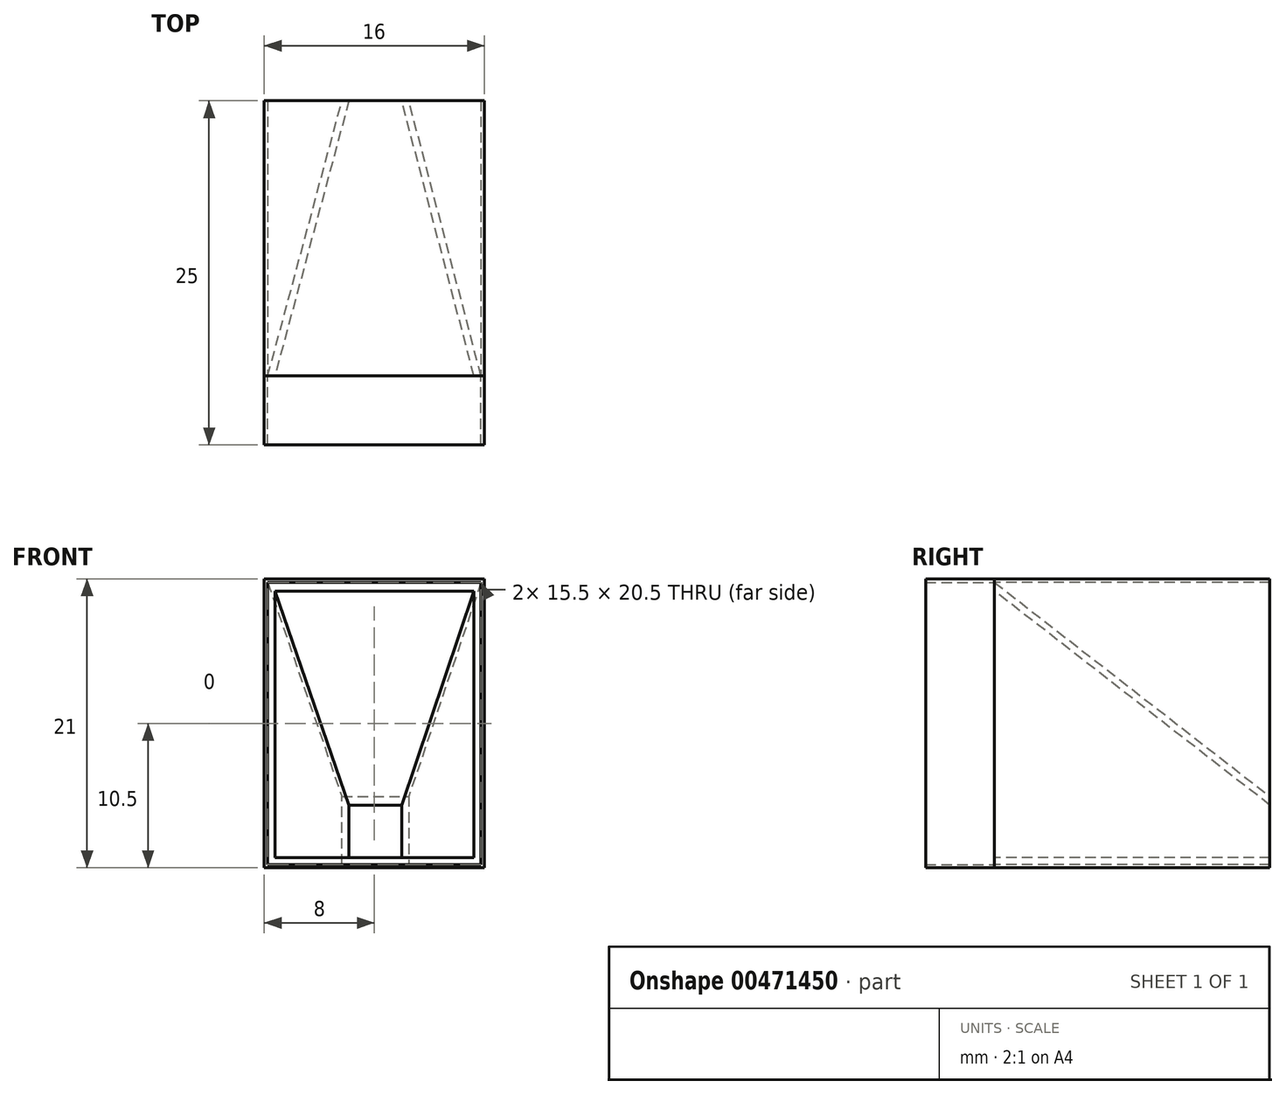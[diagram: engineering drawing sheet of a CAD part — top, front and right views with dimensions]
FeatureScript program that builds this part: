
annotation { "Feature Type Name" : "Feature", "Feature Type Description" : "" }
export const myFeature = defineFeature(function(context is Context, id is Id, definition is map)
    precondition{}
    {
        {
            var Q0;
            Q0=qCreatedBy(makeId("Front.planeOp"),FACE);
            var sketch = newSketch(context, id + "F0", { "sketchPlane" : qUnion([Q0])});
            skLineSegment(sketch, "E0.bottom", {"start": v(-8, 10.5) * mm, "end": v(8, 10.5) * mm});
            skLineSegment(sketch, "E0.top", {"start": v(-8, -10.5) * mm, "end": v(8, -10.5) * mm});
            skLineSegment(sketch, "E0.left", {"start": v(-8, 10.5) * mm, "end": v(-8, -10.5) * mm});
            skLineSegment(sketch, "E0.right", {"start": v(8, 10.5) * mm, "end": v(8, -10.5) * mm});
            skPoint(sketch, "E0.middle", {"position": v(0, 0) * mm});
            skLineSegment(sketch, "E1.bottom", {"start": v(-7.75, -10.25) * mm, "end": v(7.75, -10.25) * mm});
            skLineSegment(sketch, "E1.top", {"start": v(-7.75, 10.25) * mm, "end": v(7.75, 10.25) * mm});
            skLineSegment(sketch, "E1.left", {"start": v(-7.75, -10.25) * mm, "end": v(-7.75, 10.25) * mm});
            skLineSegment(sketch, "E1.right", {"start": v(7.75, -10.25) * mm, "end": v(7.75, 10.25) * mm});
            skSolve(sketch);
        }
        {
            var Q0;
            Q0=makeQuery(id+"F0.imprint","IMPRINT",FACE,{"disambiguationData":[TD([[makeQuery(id+"F0.imprint","IMPRINT",EDGE,{"derivedFrom":sQuery(id+"F0.wireOp",EDGE,"E0.bottom")}),-1.0]])]});
            extrude(context, id + "F1", {"entities" : qUnion([Q0]), "depth" : 5 * mm});
        }
        {
            var Q0;
            Q0=makeQuery(id+"F1.opExtrude","CAP_FACE",FACE,{"disambiguationData":[OSD([sQuery(id+"F0.wireOp",EDGE,"E0.bottom"),sQuery(id+"F0.wireOp",EDGE,"E0.top"),sQuery(id+"F0.wireOp",EDGE,"E0.left"),sQuery(id+"F0.wireOp",EDGE,"E0.right"),sQuery(id+"F0.wireOp",EDGE,"E1.bottom"),sQuery(id+"F0.wireOp",EDGE,"E1.top"),sQuery(id+"F0.wireOp",EDGE,"E1.left"),sQuery(id+"F0.wireOp",EDGE,"E1.right")])],"isStart":true});
            extrude(context, id + "F2", {"entities" : qUnion([Q0]), "depth" : 20 * mm});
        }
        {
            var Q0;
            Q0=makeQuery(id+"F2.opExtrude","CAP_FACE",FACE,{"disambiguationData":[OSD([sQuery(id+"F0.wireOp",EDGE,"E0.bottom"),sQuery(id+"F0.wireOp",EDGE,"E0.top"),sQuery(id+"F0.wireOp",EDGE,"E0.left"),sQuery(id+"F0.wireOp",EDGE,"E0.right"),sQuery(id+"F0.wireOp",EDGE,"E1.bottom"),sQuery(id+"F0.wireOp",EDGE,"E1.top"),sQuery(id+"F0.wireOp",EDGE,"E1.left"),sQuery(id+"F0.wireOp",EDGE,"E1.right")])],"isStart":false});
            var sketch = newSketch(context, id + "F3", { "sketchPlane" : qUnion([Q0])});
            skPoint(sketch, "E2.middle", {"position": v(0, -10.25) * mm});
            skLineSegment(sketch, "E3", {"start": v(2.92, -10.5) * mm, "end": v(2.92, -4.89) * mm});
            skLineSegment(sketch, "E4", {"start": v(2.92, -4.89) * mm, "end": v(-3.01, -4.89) * mm});
            skLineSegment(sketch, "E5", {"start": v(-3.01, -4.89) * mm, "end": v(-3.01, -10.5) * mm});
            skLineSegment(sketch, "E6", {"start": v(2.36, -10.25) * mm, "end": v(2.36, -5.3) * mm});
            skLineSegment(sketch, "E7", {"start": v(2.36, -5.3) * mm, "end": v(-2.5, -5.3) * mm});
            skLineSegment(sketch, "E8", {"start": v(-2.5, -5.3) * mm, "end": v(-2.5, -10.25) * mm});
            skLineSegment(sketch, "E9", {"start": v(-2.5, -10.25) * mm, "end": v(2.36, -10.25) * mm});
            skLineSegment(sketch, "E10", {"start": v(-3.01, -10.5) * mm, "end": v(2.92, -10.5) * mm});
            skSolve(sketch);
        }
        {
            var Q0;
            Q0=makeQuery(id+"F0.imprint","IMPRINT",FACE,{"disambiguationData":[TD([[makeQuery(id+"F0.imprint","IMPRINT",EDGE,{"derivedFrom":sQuery(id+"F0.wireOp",EDGE,"E1.bottom")}),1.0]])]});
            var Q1;
            Q1=makeQuery(id+"F3.imprint","IMPRINT",FACE,{"disambiguationData":[TD([[makeQuery(id+"F3.imprint","IMPRINT",EDGE,{"derivedFrom":sQuery(id+"F3.wireOp",EDGE,"E6")}),1.0]])]});
            loft(context, id + "F4", {"sheetProfilesArray" : [{ "sheetProfileEntities" : qUnion([Q0]) }, { "sheetProfileEntities" : qUnion([Q1]) }]});
        }
        {
            var Q0;
            Q0=makeQuery(id+"F4.opLoft","CAP_FACE",FACE,{"disambiguationData":[OSD([makeQuery(id+"F0.imprint","IMPRINT",FACE,{"disambiguationData":[TD([[makeQuery(id+"F0.imprint","IMPRINT",EDGE,{"derivedFrom":sQuery(id+"F0.wireOp",EDGE,"E1.bottom")}),1.0]])]})])],"isStart":true});
            var Q1;
            Q1=makeQuery(id+"F4.opLoft","CAP_FACE",FACE,{"disambiguationData":[OSD([makeQuery(id+"F3.imprint","IMPRINT",FACE,{"disambiguationData":[TD([[makeQuery(id+"F3.imprint","IMPRINT",EDGE,{"derivedFrom":sQuery(id+"F3.wireOp",EDGE,"E6")}),1.0]])]})])],"isStart":true});
            shell(context, id + "F5", {"entities" : qUnion([Q0, Q1]), "thickness" : 0.5 * mm});
        }
    });
